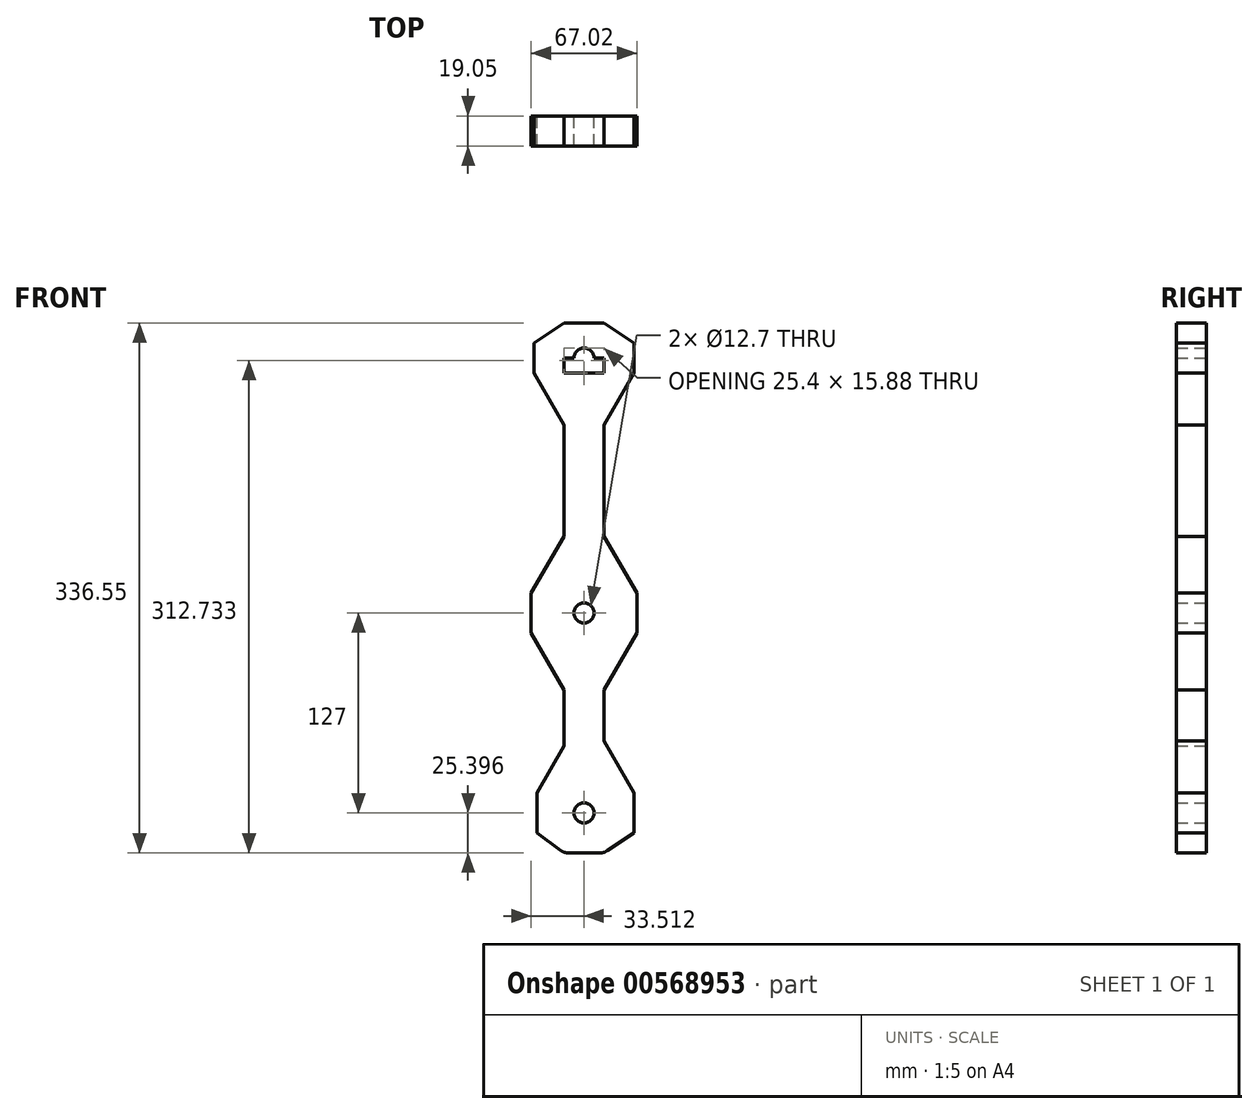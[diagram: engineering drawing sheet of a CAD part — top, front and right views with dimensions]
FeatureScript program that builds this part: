
annotation { "Feature Type Name" : "Feature", "Feature Type Description" : "" }
export const myFeature = defineFeature(function(context is Context, id is Id, definition is map)
    precondition{}
    {
        {
            var Q0;
            Q0=qCreatedBy(makeId("Front.planeOp"),FACE);
            var sketch = newSketch(context, id + "F0", { "sketchPlane" : qUnion([Q0])});
            skLineSegment(sketch, "E0.left", {"start": v(-226.26, 49) * mm, "end": v(-226.26, 29.95) * mm});
            skLineSegment(sketch, "E1.top", {"start": v(-48.46, -271.8) * mm, "end": v(-23.06, -271.8) * mm});
            skLineSegment(sketch, "E1.left", {"start": v(-48.46, 33) * mm, "end": v(-48.46, -271.8) * mm});
            skLineSegment(sketch, "E1.right", {"start": v(-23.06, 33) * mm, "end": v(-23.06, -271.8) * mm});
            skLineSegment(sketch, "E2", {"start": v(-48.46, -119.4) * mm, "end": v(-23.06, -119.4) * mm});
            skLineSegment(sketch, "E3", {"start": v(-48.46, -246.4) * mm, "end": v(-23.06, -246.4) * mm});
            skCircle(sketch, "E4", {"center": v(-35.76, -119.4) * mm, "radius": 6.35 * mm});
            skCircle(sketch, "E5", {"center": v(-35.76, -246.4) * mm, "radius": 6.35 * mm});
            skLineSegment(sketch, "E6.bottom", {"start": v(-23.06, 33) * mm, "end": v(-48.46, 33) * mm});
            skLineSegment(sketch, "E6.top", {"start": v(-23.06, 52.05) * mm, "end": v(-48.46, 52.05) * mm});
            skLineSegment(sketch, "E6.left", {"start": v(-23.06, 33) * mm, "end": v(-23.06, 52.05) * mm});
            skLineSegment(sketch, "E6.right", {"start": v(-48.46, 33) * mm, "end": v(-48.46, 52.05) * mm});
            skLineSegment(sketch, "E7", {"start": v(-35.76, 52.05) * mm, "end": v(-35.76, 33) * mm});
            skLineSegment(sketch, "E8", {"start": v(-23.06, 42.52) * mm, "end": v(-48.46, 42.52) * mm});
            skCircle(sketch, "E9", {"center": v(-35.76, 42.52) * mm, "radius": 6.35 * mm});
            skLineSegment(sketch, "E10", {"start": v(-48.46, -119.4) * mm, "end": v(-69.27, -119.4) * mm});
            skLineSegment(sketch, "E11", {"start": v(-23.06, -119.4) * mm, "end": v(-2.25, -119.4) * mm});
            skLineSegment(sketch, "E12", {"start": v(-69.27, -119.4) * mm, "end": v(-69.27, -132.1) * mm});
            skLineSegment(sketch, "E13", {"start": v(-69.27, -119.4) * mm, "end": v(-69.27, -106.7) * mm});
            skLineSegment(sketch, "E14", {"start": v(-69.27, -106.7) * mm, "end": v(-48.46, -106.7) * mm});
            skLineSegment(sketch, "E15", {"start": v(-69.27, -132.1) * mm, "end": v(-48.46, -132.1) * mm});
            skLineSegment(sketch, "E16", {"start": v(-69.27, -106.7) * mm, "end": v(-48.46, -70.66) * mm});
            skLineSegment(sketch, "E17", {"start": v(-69.27, -132.1) * mm, "end": v(-48.46, -168.15) * mm});
            skLineSegment(sketch, "E18", {"start": v(-2.25, -119.4) * mm, "end": v(-2.25, -106.7) * mm});
            skLineSegment(sketch, "E19", {"start": v(-2.25, -106.7) * mm, "end": v(-23.06, -106.7) * mm});
            skLineSegment(sketch, "E20", {"start": v(-2.25, -119.4) * mm, "end": v(-2.25, -132.1) * mm});
            skLineSegment(sketch, "E21", {"start": v(-2.25, -132.1) * mm, "end": v(-23.06, -132.1) * mm});
            skLineSegment(sketch, "E22", {"start": v(-2.25, -132.1) * mm, "end": v(-23.06, -168.15) * mm});
            skLineSegment(sketch, "E23", {"start": v(-2.25, -106.7) * mm, "end": v(-23.06, -70.66) * mm});
            skLineSegment(sketch, "E24", {"start": v(-48.46, -246.4) * mm, "end": v(-65.75, -246.4) * mm});
            skLineSegment(sketch, "E25", {"start": v(-23.06, -246.4) * mm, "end": v(-4, -246.4) * mm});
            skLineSegment(sketch, "E26.bottom", {"start": v(-65.75, -246.4) * mm, "end": v(-48.46, -246.4) * mm});
            skLineSegment(sketch, "E26.top", {"start": v(-65.75, -233.7) * mm, "end": v(-48.46, -233.7) * mm});
            skLineSegment(sketch, "E26.left", {"start": v(-65.75, -246.4) * mm, "end": v(-65.75, -233.7) * mm});
            skLineSegment(sketch, "E26.right", {"start": v(-48.46, -246.4) * mm, "end": v(-48.46, -233.7) * mm});
            skLineSegment(sketch, "E27.top", {"start": v(-65.75, -259.1) * mm, "end": v(-48.46, -259.1) * mm});
            skLineSegment(sketch, "E27.left", {"start": v(-65.75, -246.4) * mm, "end": v(-65.75, -259.1) * mm});
            skLineSegment(sketch, "E27.right", {"start": v(-48.46, -246.4) * mm, "end": v(-48.46, -259.1) * mm});
            skLineSegment(sketch, "E28.top", {"start": v(-23.06, -233.7) * mm, "end": v(-4, -233.7) * mm});
            skLineSegment(sketch, "E28.left", {"start": v(-23.06, -246.4) * mm, "end": v(-23.06, -233.7) * mm});
            skLineSegment(sketch, "E28.right", {"start": v(-4, -246.4) * mm, "end": v(-4, -233.7) * mm});
            skLineSegment(sketch, "E29.top", {"start": v(-23.06, -259.1) * mm, "end": v(-4, -259.1) * mm});
            skLineSegment(sketch, "E29.left", {"start": v(-23.06, -246.4) * mm, "end": v(-23.06, -259.1) * mm});
            skLineSegment(sketch, "E29.right", {"start": v(-4, -246.4) * mm, "end": v(-4, -259.1) * mm});
            skLineSegment(sketch, "E30", {"start": v(-65.75, -259.1) * mm, "end": v(-48.46, -271.8) * mm});
            skLineSegment(sketch, "E31", {"start": v(-65.75, -233.7) * mm, "end": v(-48.46, -203.76) * mm});
            skLineSegment(sketch, "E32", {"start": v(-4, -259.1) * mm, "end": v(-23.06, -271.8) * mm});
            skLineSegment(sketch, "E33", {"start": v(-4, -233.7) * mm, "end": v(-23.06, -200.7) * mm});
            skLineSegment(sketch, "E34", {"start": v(-48.46, 42.52) * mm, "end": v(-67.5, 42.52) * mm});
            skLineSegment(sketch, "E35", {"start": v(-23.06, 42.52) * mm, "end": v(-4, 42.52) * mm});
            skLineSegment(sketch, "E36.bottom", {"start": v(-67.5, 42.52) * mm, "end": v(-48.46, 42.52) * mm});
            skLineSegment(sketch, "E36.top", {"start": v(-67.5, 33) * mm, "end": v(-48.46, 33) * mm});
            skLineSegment(sketch, "E36.left", {"start": v(-67.5, 42.52) * mm, "end": v(-67.5, 33) * mm});
            skLineSegment(sketch, "E36.right", {"start": v(-48.46, 42.52) * mm, "end": v(-48.46, 33) * mm});
            skLineSegment(sketch, "E37.top", {"start": v(-67.5, 52.05) * mm, "end": v(-48.46, 52.05) * mm});
            skLineSegment(sketch, "E37.left", {"start": v(-67.5, 42.52) * mm, "end": v(-67.5, 52.05) * mm});
            skLineSegment(sketch, "E37.right", {"start": v(-48.46, 42.52) * mm, "end": v(-48.46, 52.05) * mm});
            skLineSegment(sketch, "E38.bottom", {"start": v(-4, 42.52) * mm, "end": v(-23.06, 42.52) * mm});
            skLineSegment(sketch, "E38.top", {"start": v(-4, 52.05) * mm, "end": v(-23.06, 52.05) * mm});
            skLineSegment(sketch, "E38.left", {"start": v(-4, 42.52) * mm, "end": v(-4, 52.05) * mm});
            skLineSegment(sketch, "E38.right", {"start": v(-23.06, 42.52) * mm, "end": v(-23.06, 52.05) * mm});
            skLineSegment(sketch, "E39.bottom", {"start": v(-23.06, 33) * mm, "end": v(-4, 33) * mm});
            skLineSegment(sketch, "E39.left", {"start": v(-23.06, 33) * mm, "end": v(-23.06, 42.52) * mm});
            skLineSegment(sketch, "E39.right", {"start": v(-4, 33) * mm, "end": v(-4, 42.52) * mm});
            skLineSegment(sketch, "E40", {"start": v(-67.5, 33) * mm, "end": v(-48.46, 0) * mm});
            skLineSegment(sketch, "E41", {"start": v(-4, 33) * mm, "end": v(-23.06, 0) * mm});
            skLineSegment(sketch, "E42.bottom", {"start": v(-48.46, 52.05) * mm, "end": v(-23.06, 52.05) * mm});
            skLineSegment(sketch, "E42.top", {"start": v(-48.46, 64.75) * mm, "end": v(-23.06, 64.75) * mm});
            skLineSegment(sketch, "E42.left", {"start": v(-48.46, 52.05) * mm, "end": v(-48.46, 64.75) * mm});
            skLineSegment(sketch, "E42.right", {"start": v(-23.06, 52.05) * mm, "end": v(-23.06, 64.75) * mm});
            skLineSegment(sketch, "E43", {"start": v(-67.5, 52.05) * mm, "end": v(-48.46, 64.75) * mm});
            skLineSegment(sketch, "E44", {"start": v(-23.06, 64.75) * mm, "end": v(-4, 52.05) * mm});
            skSolve(sketch);
        }
        {
            var Q0;
            Q0 = qSketchRegion(id + "F0", true);
            var Q1;
            {var subQ1=sQuery(id+"F0.wireOp",EDGE,"E6.top");var subQ5=sQuery(id+"F0.wireOp",EDGE,"E6.left");var subQ6=makeQuery(id+"F0.imprint","INTERSECT",VERTEX,{"derivedFrom":[subQ1,subQ5]});Q1=makeQuery(id+"F0.imprint","IMPRINT",FACE,{"disambiguationData":[TD([[makeQuery(id+"F0.imprint","IMPRINT",EDGE,{"disambiguationData":[TD([[subQ6,-1.0]])],"derivedFrom":subQ1}),1.0]])]});}
            var Q2;
            {var subQ1=sQuery(id+"F0.wireOp",EDGE,"E6.right");var subQ5=sQuery(id+"F0.wireOp",EDGE,"E6.top");var subQ6=makeQuery(id+"F0.imprint","INTERSECT",VERTEX,{"derivedFrom":[subQ5,subQ1]});Q2=makeQuery(id+"F0.imprint","IMPRINT",FACE,{"disambiguationData":[TD([[makeQuery(id+"F0.imprint","IMPRINT",EDGE,{"disambiguationData":[TD([[subQ6,1.0]])],"derivedFrom":subQ5}),1.0]])]});}
            var Q3;
            {var subQ5=sQuery(id+"F0.wireOp",EDGE,"E39.left");Q3=makeQuery(id+"F0.imprint","IMPRINT",FACE,{"disambiguationData":[TD([[makeQuery(id+"F0.imprint","IMPRINT",EDGE,{"derivedFrom":subQ5}),1.0]])]});}
            var Q4;
            {var subQ0=sQuery(id+"F0.wireOp",EDGE,"E38.right");Q4=makeQuery(id+"F0.imprint","IMPRINT",FACE,{"disambiguationData":[TD([[makeQuery(id+"F0.imprint","IMPRINT",EDGE,{"derivedFrom":subQ0}),1.0]])]});}
            var Q5;
            {var subQ5=sQuery(id+"F0.wireOp",EDGE,"E37.right");Q5=makeQuery(id+"F0.imprint","IMPRINT",FACE,{"disambiguationData":[TD([[makeQuery(id+"F0.imprint","IMPRINT",EDGE,{"derivedFrom":subQ5}),-1.0]])]});}
            var Q6;
            {var subQ5=sQuery(id+"F0.wireOp",EDGE,"E36.right");Q6=makeQuery(id+"F0.imprint","IMPRINT",FACE,{"disambiguationData":[TD([[makeQuery(id+"F0.imprint","IMPRINT",EDGE,{"derivedFrom":subQ5}),1.0]])]});}
            extrude(context, id + "F1", {"entities" : qUnion([Q0, Q1, Q2, Q3, Q4, Q5, Q6]), "depth" : 19.05 * mm, "offsetDistance" : 25.4 * mm});
        }
        {
            var Q0;
            Q0=makeQuery(id+"F1.opExtrude","SWEPT_EDGE",EDGE,{"disambiguationData":[OSD([sQuery(id+"F0.wireOp",EDGE,"E1.top"),sQuery(id+"F0.wireOp",EDGE,"E1.right")])]});
            var Q1;
            Q1=makeQuery(id+"F1.opExtrude","SWEPT_EDGE",EDGE,{"disambiguationData":[OSD([sQuery(id+"F0.wireOp",EDGE,"E1.top"),sQuery(id+"F0.wireOp",EDGE,"E1.left")])]});
            var Q2;
            Q2=makeQuery(id+"F1.opExtrude","SWEPT_EDGE",EDGE,{"disambiguationData":[OSD([sQuery(id+"F0.wireOp",EDGE,"62Zb3wu4-qX6k-R4AG-71GD-BKjphRurf9Ob.top"),sQuery(id+"F0.wireOp",EDGE,"62Zb3wu4-qX6k-R4AG-71GD-BKjphRurf9Ob.left")])]});
            var Q3;
            Q3=makeQuery(id+"F1.opExtrude","SWEPT_EDGE",EDGE,{"disambiguationData":[OSD([sQuery(id+"F0.wireOp",EDGE,"62Zb3wu4-qX6k-R4AG-71GD-BKjphRurf9Ob.top"),sQuery(id+"F0.wireOp",EDGE,"62Zb3wu4-qX6k-R4AG-71GD-BKjphRurf9Ob.right")])]});
            fillet(context, id + "F2", {"entities" : qUnion([Q0, Q1, Q2, Q3]), "radius" : 8.9 * mm, "tangentPropagation" : true, "allowEdgeOverflow" : false});
        }
    });
